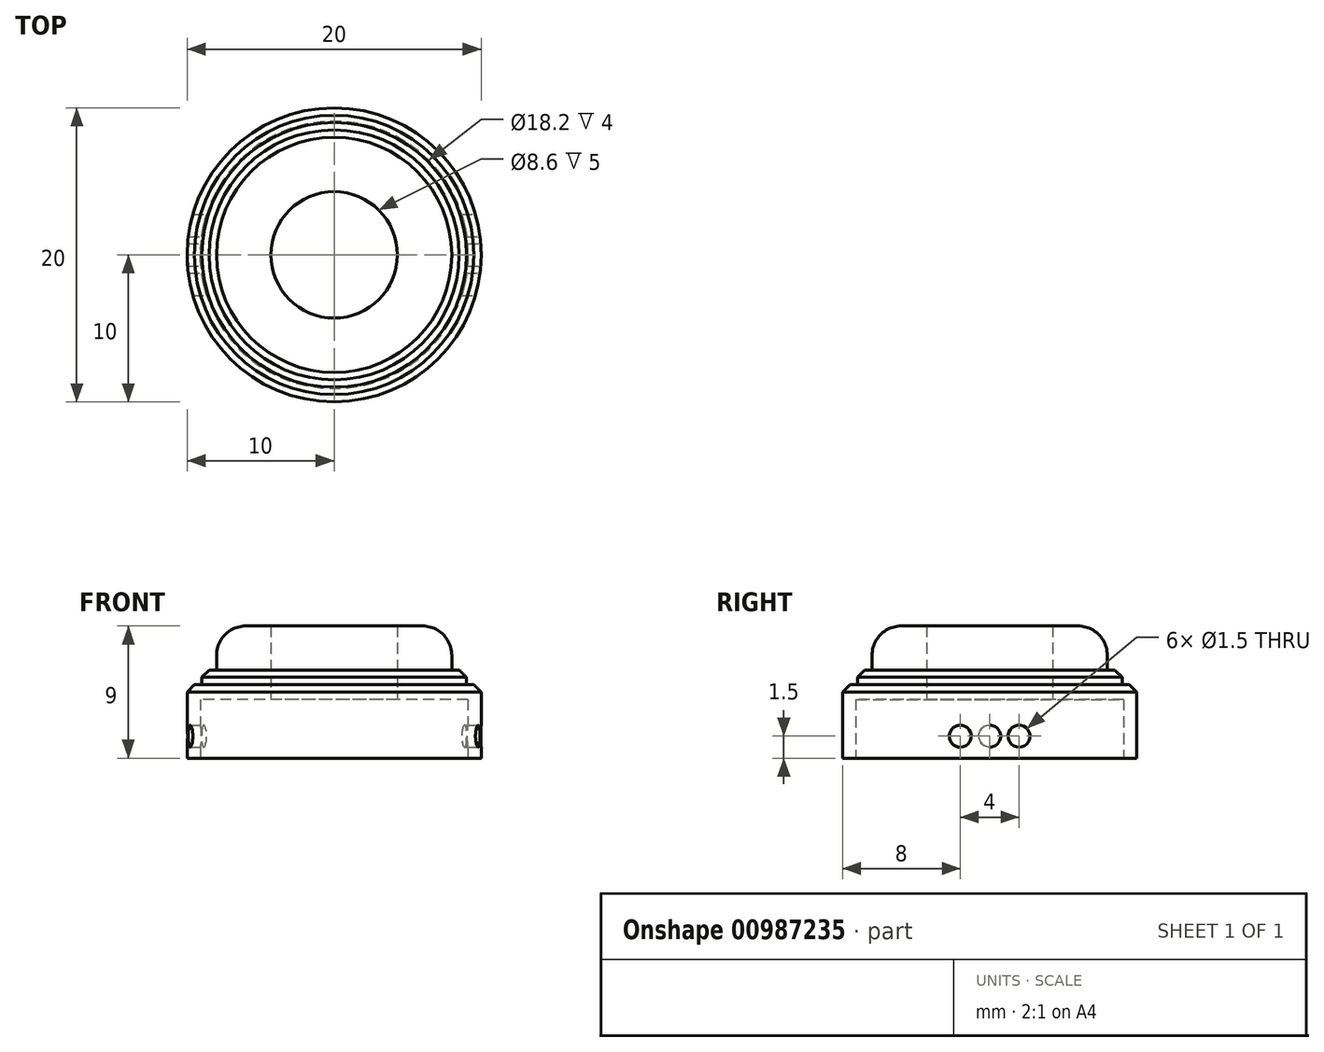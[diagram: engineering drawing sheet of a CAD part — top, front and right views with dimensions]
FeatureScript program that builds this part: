
annotation { "Feature Type Name" : "Feature", "Feature Type Description" : "" }
export const myFeature = defineFeature(function(context is Context, id is Id, definition is map)
    precondition{}
    {
        {
            var Q0;
            Q0=qCreatedBy(makeId("Top.planeOp"),FACE);
            var sketch = newSketch(context, id + "F0", { "sketchPlane" : qUnion([Q0])});
            skCircle(sketch, "E0", {"center": v(0, 0) * mm, "radius": 10 * mm});
            skCircle(sketch, "E1", {"center": v(0, 0) * mm, "radius": 9.1 * mm});
            skSolve(sketch);
        }
        {
            var Q0;
            Q0=makeQuery(id+"F0.imprint","IMPRINT",FACE,{"disambiguationData":[TD([[makeQuery(id+"F0.imprint","IMPRINT",EDGE,{"derivedFrom":sQuery(id+"F0.wireOp",EDGE,"E0")}),1.0]])]});
            extrude(context, id + "F1", {"entities" : qUnion([Q0]), "depth" : 4 * mm, "offsetDistance" : 25 * mm});
        }
        {
            var Q0;
            Q0=qCreatedBy(makeId("Right.planeOp"),FACE);
            var sketch = newSketch(context, id + "F2", { "sketchPlane" : qUnion([Q0])});
            skLineSegment(sketch, "E2", {"start": v(0, 0) * mm, "end": v(0, 1.5) * mm});
            skLineSegment(sketch, "E3", {"start": v(-2, 1.5) * mm, "end": v(2, 1.5) * mm});
            skCircle(sketch, "E4", {"center": v(-2, 1.5) * mm, "radius": 0.75 * mm});
            skCircle(sketch, "E5", {"center": v(0, 1.5) * mm, "radius": 0.75 * mm});
            skCircle(sketch, "E6", {"center": v(2, 1.5) * mm, "radius": 0.75 * mm});
            skSolve(sketch);
        }
        {
            var Q0;
            {var subQ0=sQuery(id+"F2.wireOp",EDGE,"E3");var subQ1=sQuery(id+"F2.wireOp",EDGE,"E2");var subQ2=makeQuery(id+"F2.imprint","INTERSECT",VERTEX,{"derivedFrom":[subQ1,subQ0]});Q0=makeQuery(id+"F2.imprint","IMPRINT",FACE,{"disambiguationData":[TD([[makeQuery(id+"F2.imprint","IMPRINT",EDGE,{"disambiguationData":[TD([[subQ2,1.0]])],"derivedFrom":subQ1}),1.0]])]});}
            var Q1;
            {var subQ0=sQuery(id+"F2.wireOp",EDGE,"E3");var subQ1=sQuery(id+"F2.wireOp",EDGE,"E2");var subQ2=makeQuery(id+"F2.imprint","INTERSECT",VERTEX,{"derivedFrom":[subQ1,subQ0]});Q1=makeQuery(id+"F2.imprint","IMPRINT",FACE,{"disambiguationData":[TD([[makeQuery(id+"F2.imprint","IMPRINT",EDGE,{"disambiguationData":[TD([[subQ2,1.0]])],"derivedFrom":subQ1}),-1.0]])]});}
            var Q2;
            {var subQ0=sQuery(id+"F2.wireOp",EDGE,"E3");var subQ1=makeQuery(id+"F2.imprint","INTERSECT",VERTEX,{"derivedFrom":[sQuery(id+"F2.wireOp",EDGE,"E2"),subQ0]});Q2=makeQuery(id+"F2.imprint","IMPRINT",FACE,{"disambiguationData":[TD([[makeQuery(id+"F2.imprint","IMPRINT",EDGE,{"disambiguationData":[TD([[subQ1,1.0]])],"derivedFrom":subQ0}),1.0]])]});}
            var Q3;
            Q3=makeQuery(id+"F2.imprint","IMPRINT",FACE,{"disambiguationData":[TD([[makeQuery(id+"F2.imprint","IMPRINT",EDGE,{"derivedFrom":sQuery(id+"F2.wireOp",EDGE,"E4")}),1.0]])]});
            var Q4;
            Q4=makeQuery(id+"F2.imprint","IMPRINT",FACE,{"disambiguationData":[TD([[makeQuery(id+"F2.imprint","IMPRINT",EDGE,{"derivedFrom":sQuery(id+"F2.wireOp",EDGE,"E6")}),1.0]])]});
            extrude(context, id + "F3", {"entities" : qUnion([Q0, Q1, Q2, Q3, Q4]), "operationType" : NewBodyOperationType.REMOVE, "oppositeDirection" : true, "depth" : 25 * mm, "offsetDistance" : 25 * mm, "hasSecondDirection" : true, "secondDirectionOppositeDirection" : false, "secondDirectionDepth" : 25 * mm});
        }
        {
            var Q0;
            Q0=makeQuery(id+"F1.opExtrude","CAP_FACE",FACE,{"disambiguationData":[OSD([sQuery(id+"F0.wireOp",EDGE,"E0"),sQuery(id+"F0.wireOp",EDGE,"E1")])],"isStart":false});
            var sketch = newSketch(context, id + "F4", { "sketchPlane" : qUnion([Q0])});
            skCircle(sketch, "E7", {"center": v(0, 0) * mm, "radius": 10 * mm});
            skCircle(sketch, "E8", {"center": v(0, 0) * mm, "radius": 9 * mm});
            skCircle(sketch, "E9", {"center": v(0, 0) * mm, "radius": 8 * mm});
            skCircle(sketch, "E10", {"center": v(0, 0) * mm, "radius": 4.3 * mm});
            skSolve(sketch);
        }
        {
            var Q0;
            Q0=makeQuery(id+"F4.imprint","IMPRINT",FACE,{"disambiguationData":[TD([[makeQuery(id+"F4.imprint","IMPRINT",EDGE,{"derivedFrom":sQuery(id+"F4.wireOp",EDGE,"E7")}),1.0]])]});
            var Q1;
            Q1=makeQuery(id+"F4.imprint","IMPRINT",FACE,{"disambiguationData":[TD([[makeQuery(id+"F4.imprint","IMPRINT",EDGE,{"derivedFrom":sQuery(id+"F4.wireOp",EDGE,"E8")}),1.0]])]});
            var Q2;
            Q2=makeQuery(id+"F4.imprint","IMPRINT",FACE,{"disambiguationData":[TD([[makeQuery(id+"F4.imprint","IMPRINT",EDGE,{"derivedFrom":sQuery(id+"F4.wireOp",EDGE,"E8")}),-1.0]])]});
            var Q3;
            Q3=makeQuery(id+"F4.imprint","IMPRINT",FACE,{"disambiguationData":[TD([[makeQuery(id+"F4.imprint","IMPRINT",EDGE,{"derivedFrom":sQuery(id+"F4.wireOp",EDGE,"E9")}),1.0]])]});
            extrude(context, id + "F5", {"entities" : qUnion([Q0, Q1, Q2, Q3]), "operationType" : NewBodyOperationType.ADD, "depth" : 1 * mm, "offsetDistance" : 25 * mm});
        }
        {
            var Q0;
            Q0=makeQuery(id+"F4.imprint","IMPRINT",FACE,{"disambiguationData":[TD([[makeQuery(id+"F4.imprint","IMPRINT",EDGE,{"derivedFrom":sQuery(id+"F4.wireOp",EDGE,"E8")}),1.0]])]});
            var Q1;
            Q1=makeQuery(id+"F4.imprint","IMPRINT",FACE,{"disambiguationData":[TD([[makeQuery(id+"F4.imprint","IMPRINT",EDGE,{"derivedFrom":sQuery(id+"F4.wireOp",EDGE,"E9")}),1.0]])]});
            extrude(context, id + "F6", {"entities" : qUnion([Q0, Q1]), "operationType" : NewBodyOperationType.ADD, "depth" : 2 * mm, "offsetDistance" : 25 * mm});
        }
        {
            var Q0;
            Q0=makeQuery(id+"F4.imprint","IMPRINT",FACE,{"disambiguationData":[TD([[makeQuery(id+"F4.imprint","IMPRINT",EDGE,{"derivedFrom":sQuery(id+"F4.wireOp",EDGE,"E9")}),1.0]])]});
            extrude(context, id + "F7", {"entities" : qUnion([Q0]), "operationType" : NewBodyOperationType.ADD, "depth" : 5 * mm, "offsetDistance" : 25 * mm});
        }
        {
            var Q0;
            Q0=makeQuery(id+"F5.opExtrude","CAP_EDGE",EDGE,{"disambiguationData":[OSD([sQuery(id+"F4.wireOp",EDGE,"E7")])],"isStart":false});
            var Q1;
            Q1=makeQuery(id+"F6.opExtrude","CAP_EDGE",EDGE,{"disambiguationData":[OSD([sQuery(id+"F4.wireOp",EDGE,"E8")])],"isStart":false});
            chamfer(context, id + "F8", {"entities" : qUnion([Q0, Q1]), "width" : .5 * mm, "tangentPropagation" : true});
        }
        {
            var Q0;
            Q0=makeQuery(id+"F7.opExtrude","CAP_EDGE",EDGE,{"disambiguationData":[OSD([sQuery(id+"F4.wireOp",EDGE,"E9")])],"isStart":false});
            fillet(context, id + "F9", {"entities" : qUnion([Q0]), "radius" : 2 * mm, "tangentPropagation" : true, "allowEdgeOverflow" : false});
        }
    });
